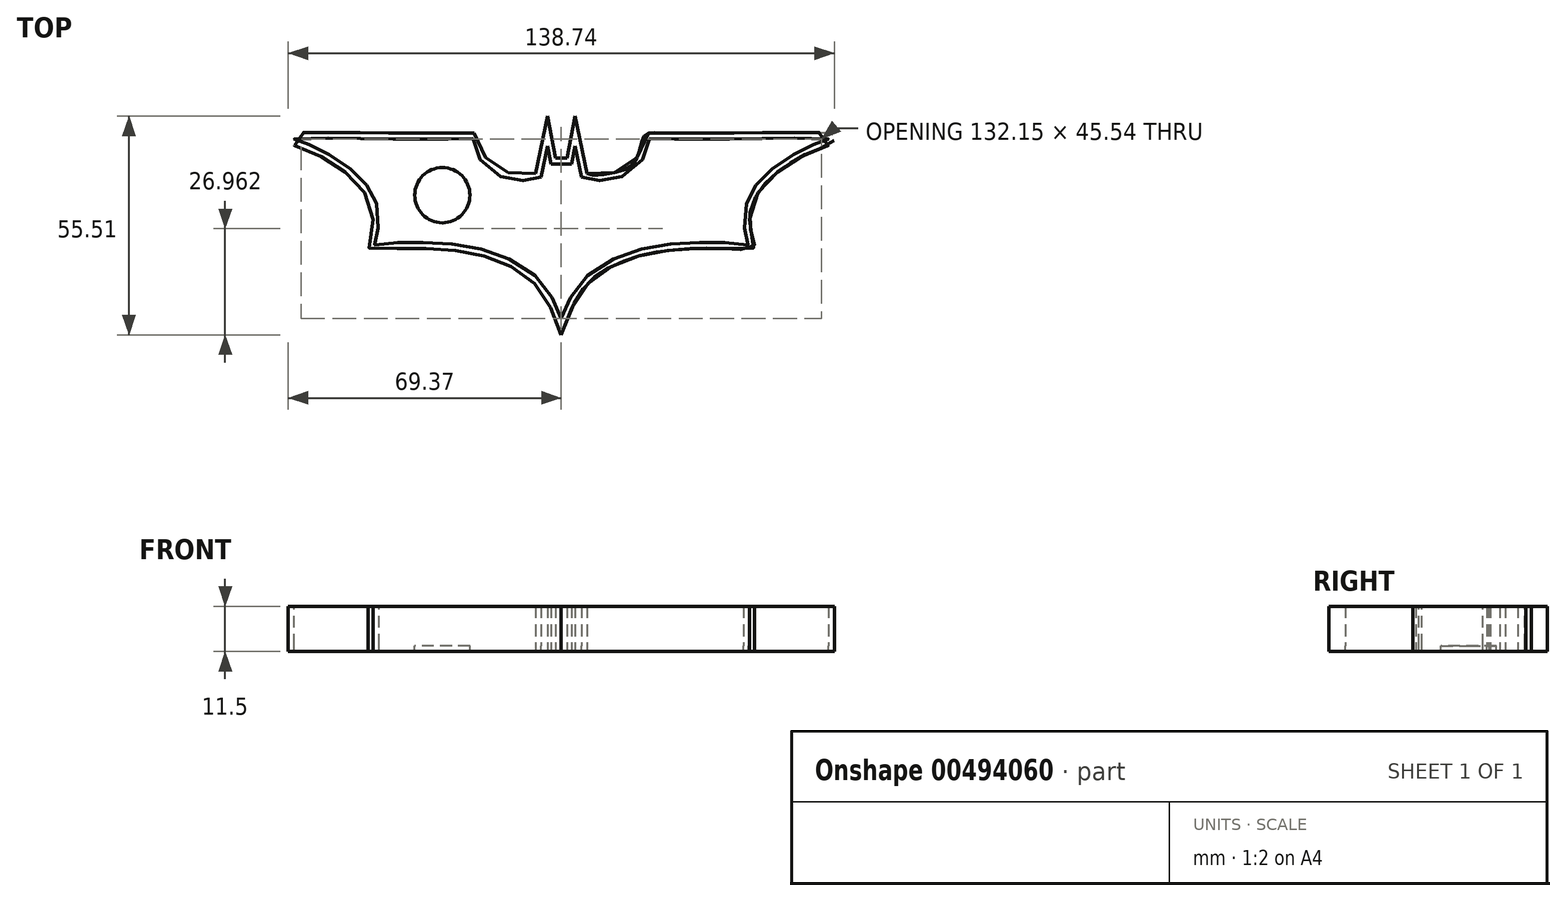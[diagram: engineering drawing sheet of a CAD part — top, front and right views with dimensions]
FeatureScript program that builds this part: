
annotation { "Feature Type Name" : "Feature", "Feature Type Description" : "" }
export const myFeature = defineFeature(function(context is Context, id is Id, definition is map)
    precondition{}
    {
        {
            var Q0;
            Q0=qCreatedBy(makeId("Top.planeOp"),FACE);
            var sketch = newSketch(context, id + "F0", { "sketchPlane" : qUnion([Q0])});
            skLineSegment(sketch, "E0", {"start": v(0, 38.5) * mm, "end": v(-2.64, 38.5) * mm});
            skLineSegment(sketch, "E1", {"start": v(-2.64, 38.5) * mm, "end": v(-3.55, 43.08) * mm});
            skLineSegment(sketch, "E2", {"start": v(-3.55, 43.08) * mm, "end": v(-5.16, 35.21) * mm});
            skLineSegment(sketch, "E3.MirrorCS", {"start": v(3.55, 43.08) * mm, "end": v(5.16, 35.21) * mm});
            skLineSegment(sketch, "E4.MirrorCS", {"start": v(2.64, 38.5) * mm, "end": v(3.55, 43.08) * mm});
            skLineSegment(sketch, "E5.MirrorCS", {"start": v(0, 38.5) * mm, "end": v(2.64, 38.5) * mm});
            skFitSpline(sketch, "E6", {"points": [v(-5.16, 35.21) * mm, v(-8.49, 34.23) * mm, v(-13.35, 34.83) * mm, v(-19.66, 37.98) * mm, v(-22.22, 44.72) * mm, v(-22.82, 44.98) * mm, v(-41.25, 44.9) * mm, v(-67.86, 44.9) * mm, v(-67.6, 44.72) * mm, v(-63.6, 43.27) * mm, v(-58.9, 40.97) * mm, v(-53.02, 36.87) * mm, v(-49.43, 33.12) * mm, v(-47.13, 28.86) * mm, v(-46.45, 22.71) * mm, v(-47.56, 18.02) * mm, v(-47.3, 18.02) * mm, v(-41.07, 18.62) * mm, v(-34.34, 18.62) * mm, v(-25.12, 17.85) * mm, v(-16.34, 15.63) * mm, v(-7.47, 10.94) * mm, v(-2.18, 4.29) * mm, v(0, -0.66) * mm], "startDerivative": vector(-75.36, -70.94) * mm, "endDerivative": vector(44.22, -115.37) * mm});
            skFitSpline(sketch, "E7.MirrorCS", {"points": [v(5.16, 35.21) * mm, v(8.49, 34.23) * mm, v(13.35, 34.83) * mm, v(19.66, 37.98) * mm, v(22.22, 44.72) * mm, v(22.82, 44.98) * mm, v(41.25, 44.9) * mm, v(67.86, 44.9) * mm, v(67.6, 44.72) * mm, v(63.6, 43.27) * mm, v(58.9, 40.97) * mm, v(53.02, 36.87) * mm, v(49.43, 33.12) * mm, v(47.13, 28.86) * mm, v(46.45, 22.71) * mm, v(47.56, 18.02) * mm, v(47.3, 18.02) * mm, v(41.07, 18.62) * mm, v(34.34, 18.62) * mm, v(25.12, 17.85) * mm, v(16.34, 15.63) * mm, v(7.47, 10.94) * mm, v(2.18, 4.29) * mm, v(0, -0.66) * mm], "startDerivative": vector(75.36, -70.94) * mm, "endDerivative": vector(-44.22, -115.37) * mm});
            skSolve(sketch);
        }
        {
            var Q0;
            Q0=makeQuery(id+"F0.imprint","IMPRINT",FACE,{"disambiguationData":[TD([[makeQuery(id+"F0.imprint","IMPRINT",EDGE,{"derivedFrom":sQuery(id+"F0.wireOp",EDGE,"E0")}),1.0]])]});
            extrude(context, id + "F1", {"entities" : qUnion([Q0]), "depth" : 10 * mm});
        }
        {
            var Q0;
            Q0=makeQuery(id+"F1.opExtrude","CAP_FACE",FACE,{"disambiguationData":[OSD([sQuery(id+"F0.wireOp",EDGE,"E0"),sQuery(id+"F0.wireOp",EDGE,"E1"),sQuery(id+"F0.wireOp",EDGE,"E2"),sQuery(id+"F0.wireOp",EDGE,"E3.MirrorCS"),sQuery(id+"F0.wireOp",EDGE,"E4.MirrorCS"),sQuery(id+"F0.wireOp",EDGE,"E5.MirrorCS"),sQuery(id+"F0.wireOp",EDGE,"E6"),sQuery(id+"F0.wireOp",EDGE,"E7.MirrorCS")])],"isStart":false});
            shell(context, id + "F2", {"entities" : qUnion([Q0]), "thickness" : 1.5 * mm, "oppositeDirection" : true});
        }
        {
            var Q0;
            Q0=makeQuery(id+"F2.opShell","OFFSET_FACE",FACE,{"disambiguationData":[OSD([sQuery(id+"F0.wireOp",EDGE,"E0"),sQuery(id+"F0.wireOp",EDGE,"E1"),sQuery(id+"F0.wireOp",EDGE,"E2"),sQuery(id+"F0.wireOp",EDGE,"E3.MirrorCS"),sQuery(id+"F0.wireOp",EDGE,"E4.MirrorCS"),sQuery(id+"F0.wireOp",EDGE,"E5.MirrorCS"),sQuery(id+"F0.wireOp",EDGE,"E6"),sQuery(id+"F0.wireOp",EDGE,"E7.MirrorCS")])]});
            var sketch = newSketch(context, id + "F3", { "sketchPlane" : qUnion([Q0])});
            skCircle(sketch, "E8", {"center": v(0, 22.78) * mm, "radius": 7.35 * mm});
            skCircle(sketch, "E9", {"center": v(30.22, 30.6) * mm, "radius": 7.02 * mm});
            skCircle(sketch, "E10.MirrorC", {"center": v(-30.22, 30.6) * mm, "radius": 7.02 * mm});
            skSolve(sketch);
        }
        {
            var Q0;
            Q0=makeQuery(id+"F3.imprint","IMPRINT",FACE,{"disambiguationData":[TD([[makeQuery(id+"F3.imprint","IMPRINT",EDGE,{"derivedFrom":sQuery(id+"F3.wireOp",EDGE,"E8")}),1.0]])]});
            extrude(context, id + "F4", {"entities" : qUnion([Q0]), "operationType" : NewBodyOperationType.REMOVE, "oppositeDirection" : true, "depth" : 12.7 * mm});
        }
        {
            var Q0;
            Q0=makeQuery(id+"F3.imprint","IMPRINT",FACE,{"disambiguationData":[TD([[makeQuery(id+"F3.imprint","IMPRINT",EDGE,{"derivedFrom":sQuery(id+"F3.wireOp",EDGE,"E10.MirrorC")}),-1.0]])]});
            var Q1;
            Q1=makeQuery(id+"F3.imprint","IMPRINT",FACE,{"disambiguationData":[TD([[makeQuery(id+"F3.imprint","IMPRINT",EDGE,{"derivedFrom":sQuery(id+"F3.wireOp",EDGE,"E9")}),1.0]])]});
            var Q2;
            Q2=makeQuery(id+"F3.imprint","IMPRINT",FACE,{"disambiguationData":[TD([[makeQuery(id+"F3.imprint","IMPRINT",EDGE,{"derivedFrom":sQuery(id+"F3.wireOp",EDGE,"E8")}),1.0]])]});
            extrude(context, id + "F5", {"entities" : qUnion([Q0, Q1, Q2]), "operationType" : NewBodyOperationType.REMOVE, "oppositeDirection" : true, "depth" : 15.1 * mm});
        }
    });
